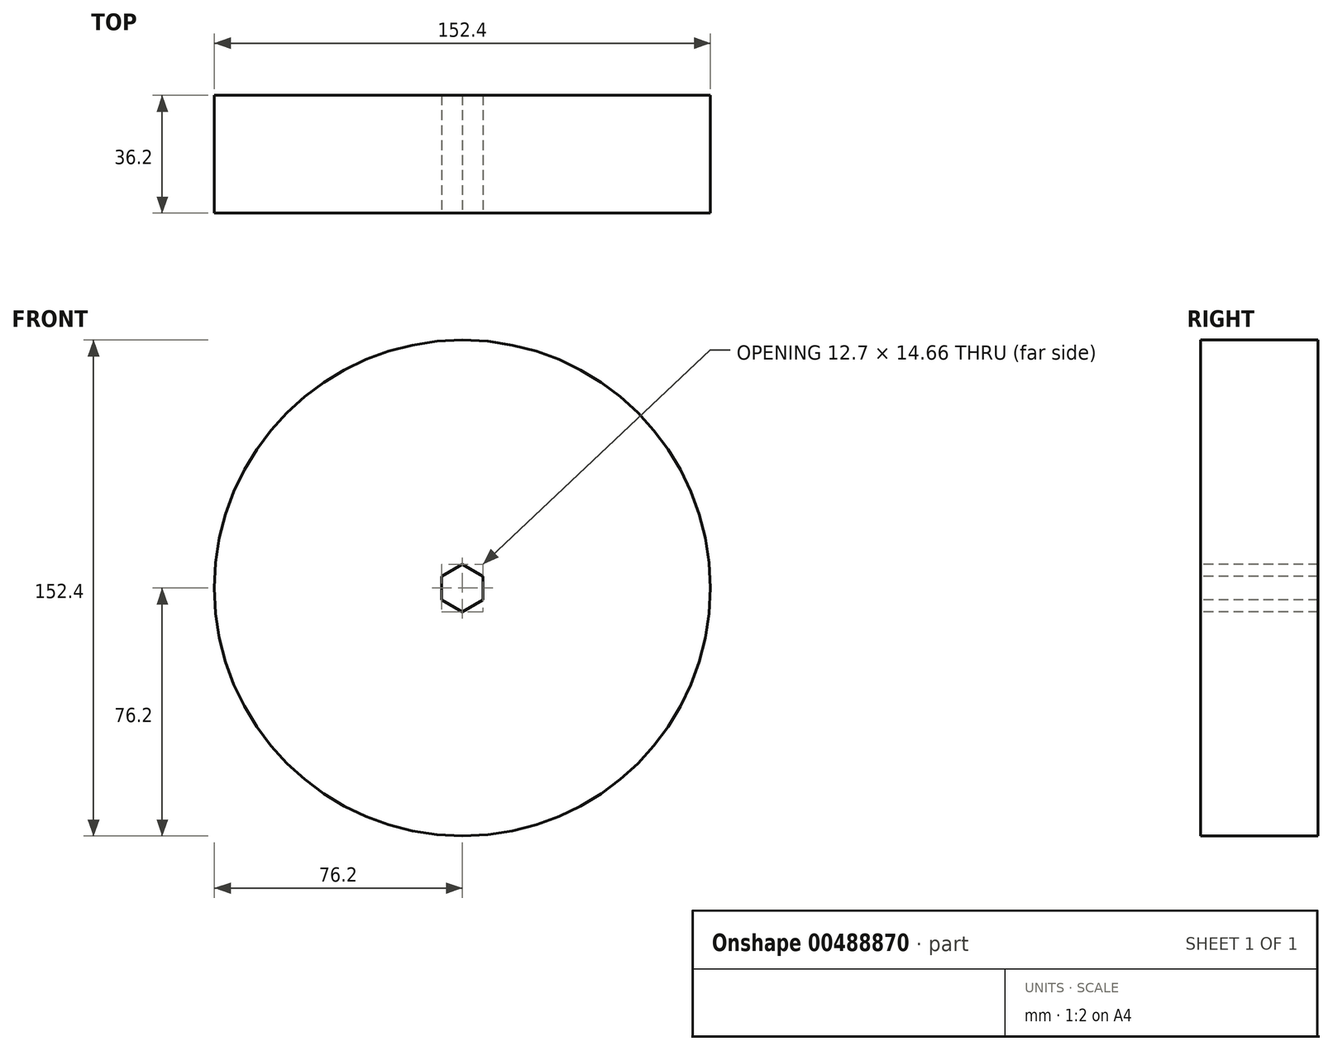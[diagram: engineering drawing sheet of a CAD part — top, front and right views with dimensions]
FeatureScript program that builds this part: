
annotation { "Feature Type Name" : "Feature", "Feature Type Description" : "" }
export const myFeature = defineFeature(function(context is Context, id is Id, definition is map)
    precondition{}
    {
        {
            var Q0;
            Q0=qCreatedBy(makeId("Front.planeOp"),FACE);
            var sketch = newSketch(context, id + "F0", { "sketchPlane" : qUnion([Q0])});
            skCircle(sketch, "E0", {"center": v(0, 0) * mm, "radius": 76.2 * mm});
            skSolve(sketch);
        }
        {
            var Q0;
            Q0=makeQuery(id+"F0.imprint","IMPRINT",FACE,{"disambiguationData":[TD([[makeQuery(id+"F0.imprint","IMPRINT",EDGE,{"derivedFrom":sQuery(id+"F0.wireOp",EDGE,"E0")}),1.0]])]});
            var Q1;
            Q1=sQuery(id+"F0.wireOp",EDGE,"E0");
            extrude(context, id + "F1", {"entities" : qUnion([Q0]), "surfaceEntities" : qUnion([Q1]), "depth" : 36.2 * mm, "offsetDistance" : 25.4 * mm});
        }
        {
            var Q0;
            Q0=makeQuery(id+"F1.opExtrude","CAP_FACE",FACE,{"disambiguationData":[OSD([sQuery(id+"F0.wireOp",EDGE,"E0")])],"isStart":false});
            var sketch = newSketch(context, id + "F2", { "sketchPlane" : qUnion([Q0])});
            skLineSegment(sketch, "E1.0", {"start": v(0, 7.33) * mm, "end": v(6.35, 3.67) * mm});
            skLineSegment(sketch, "E1.1", {"start": v(6.35, 3.67) * mm, "end": v(6.35, -3.67) * mm});
            skLineSegment(sketch, "E1.2", {"start": v(6.35, -3.67) * mm, "end": v(0, -7.33) * mm});
            skLineSegment(sketch, "E1.3", {"start": v(0, -7.33) * mm, "end": v(-6.35, -3.67) * mm});
            skLineSegment(sketch, "E1.4", {"start": v(-6.35, -3.67) * mm, "end": v(-6.35, 3.67) * mm});
            skLineSegment(sketch, "E1.5", {"start": v(-6.35, 3.67) * mm, "end": v(0, 7.33) * mm});
            skSolve(sketch);
        }
        {
            var Q0;
            Q0=makeQuery(id+"F2.imprint","IMPRINT",FACE,{"disambiguationData":[TD([[makeQuery(id+"F2.imprint","IMPRINT",EDGE,{"derivedFrom":sQuery(id+"F2.wireOp",EDGE,"E1.0")}),-1.0]])]});
            extrude(context, id + "F3", {"entities" : qUnion([Q0]), "operationType" : NewBodyOperationType.REMOVE, "oppositeDirection" : true, "depth" : 76.2 * mm, "offsetDistance" : 25.4 * mm});
        }
    });
